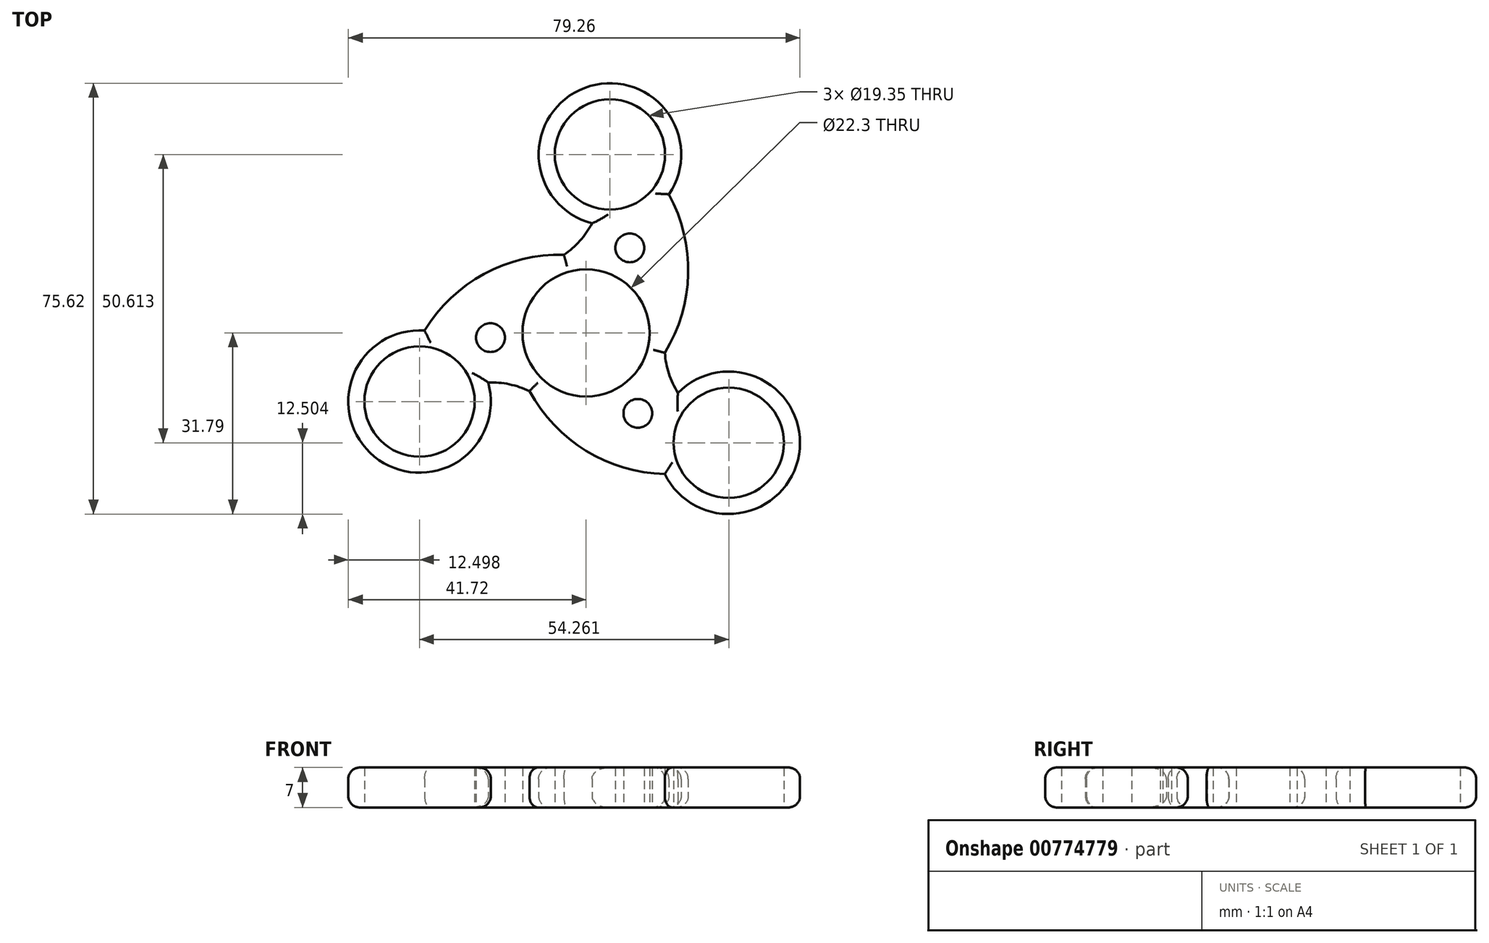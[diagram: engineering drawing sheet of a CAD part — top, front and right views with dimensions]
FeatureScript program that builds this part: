
annotation { "Feature Type Name" : "Feature", "Feature Type Description" : "" }
export const myFeature = defineFeature(function(context is Context, id is Id, definition is map)
    precondition{}
    {
        {
            var Q0;
            Q0=qCreatedBy(makeId("Top.planeOp"),FACE);
            var sketch = newSketch(context, id + "F0", { "sketchPlane" : qUnion([Q0])});
            skCircle(sketch, "E0", {"center": v(0, 0) * mm, "radius": 11.15 * mm});
            skArc(sketch, "E1", {"start": v(-9.94, -10.23) * mm, "mid": v(-0.01, -20.67) * mm, "end": v(13.8, -24.76) * mm});
            skArc(sketch, "E2", {"start": v(13.83, -3.5) * mm, "mid": v(14.54, -7.15) * mm, "end": v(16.13, -10.52) * mm});
            skCircle(sketch, "E3", {"center": v(25.04, -19.29) * mm, "radius": 9.68 * mm});
            skArc(sketch, "E4", {"start": v(13.8, -24.76) * mm, "mid": v(37.38, -21.3) * mm, "end": v(16.13, -10.52) * mm});
            skArc(sketch, "E5.1.0", {"start": v(-3.9, 13.72) * mm, "mid": v(-1.08, 16.16) * mm, "end": v(1.05, 19.23) * mm});
            skCircle(sketch, "E5.1.1", {"center": v(4.18, 31.33) * mm, "radius": 9.68 * mm});
            skArc(sketch, "E5.1.2", {"start": v(14.54, 24.34) * mm, "mid": v(-0.24, 43.02) * mm, "end": v(1.05, 19.23) * mm});
            skArc(sketch, "E5.1.3", {"start": v(13.83, -3.5) * mm, "mid": v(17.91, 10.33) * mm, "end": v(14.54, 24.34) * mm});
            skArc(sketch, "E5.2.0", {"start": v(-9.94, -10.23) * mm, "mid": v(-13.46, -9.01) * mm, "end": v(-17.17, -8.7) * mm});
            skCircle(sketch, "E5.2.1", {"center": v(-29.22, -12.04) * mm, "radius": 9.68 * mm});
            skArc(sketch, "E5.2.2", {"start": v(-28.35, 0.43) * mm, "mid": v(-37.13, -21.72) * mm, "end": v(-17.17, -8.7) * mm});
            skArc(sketch, "E5.2.3", {"start": v(-3.9, 13.72) * mm, "mid": v(-17.9, 10.35) * mm, "end": v(-28.35, 0.43) * mm});
            skPoint(sketch, "E6.trimOffspring.end.orphan", {"position": v(14, 0) * mm});
            skPoint(sketch, "E7.orphan", {"position": v(13.34, -4.26) * mm});
            skPoint(sketch, "E8.orphan", {"position": v(-7, -12.12) * mm});
            skPoint(sketch, "E9.orphan", {"position": v(-10.36, -9.42) * mm});
            skPoint(sketch, "E10.orphan", {"position": v(-7, 12.12) * mm});
            skPoint(sketch, "E11.orphan", {"position": v(-2.98, 13.68) * mm});
            skCircle(sketch, "E12", {"center": v(7.68, 14.94) * mm, "radius": 2.53 * mm});
            skCircle(sketch, "E13.1.0", {"center": v(-16.78, -0.82) * mm, "radius": 2.53 * mm});
            skCircle(sketch, "E13.2.0", {"center": v(9.1, -14.12) * mm, "radius": 2.53 * mm});
            skSolve(sketch);
        }
        {
            var Q0;
            Q0 = qSketchRegion(id + "F0", true);
            extrude(context, id + "F1", {"entities" : qUnion([Q0]), "depth" : 7 * mm, "offsetDistance" : 25 * mm});
        }
        {
            var Q0;
            Q0=makeQuery(id+"F1.opExtrude","CAP_EDGE",EDGE,{"disambiguationData":[OSD([sQuery(id+"F0.wireOp",EDGE,"E5.2.2")])],"isStart":false});
            var Q1;
            Q1=makeQuery(id+"F1.opExtrude","CAP_EDGE",EDGE,{"disambiguationData":[OSD([sQuery(id+"F0.wireOp",EDGE,"E5.2.2")])],"isStart":true});
            var Q2;
            Q2=makeQuery(id+"F1.opExtrude","CAP_EDGE",EDGE,{"disambiguationData":[OSD([sQuery(id+"F0.wireOp",EDGE,"E5.2.0")])],"isStart":true});
            var Q3;
            Q3=makeQuery(id+"F1.opExtrude","CAP_EDGE",EDGE,{"disambiguationData":[OSD([sQuery(id+"F0.wireOp",EDGE,"E5.2.0")])],"isStart":false});
            var Q4;
            Q4=makeQuery(id+"F1.opExtrude","CAP_EDGE",EDGE,{"disambiguationData":[OSD([sQuery(id+"F0.wireOp",EDGE,"E1")])],"isStart":false});
            var Q5;
            Q5=makeQuery(id+"F1.opExtrude","CAP_EDGE",EDGE,{"disambiguationData":[OSD([sQuery(id+"F0.wireOp",EDGE,"E4")])],"isStart":true});
            var Q6;
            Q6=makeQuery(id+"F1.opExtrude","CAP_EDGE",EDGE,{"disambiguationData":[OSD([sQuery(id+"F0.wireOp",EDGE,"E4")])],"isStart":false});
            var Q7;
            Q7=makeQuery(id+"F1.opExtrude","CAP_EDGE",EDGE,{"disambiguationData":[OSD([sQuery(id+"F0.wireOp",EDGE,"E2")])],"isStart":false});
            var Q8;
            Q8=makeQuery(id+"F1.opExtrude","CAP_EDGE",EDGE,{"disambiguationData":[OSD([sQuery(id+"F0.wireOp",EDGE,"E5.1.3")])],"isStart":false});
            var Q9;
            Q9=makeQuery(id+"F1.opExtrude","CAP_EDGE",EDGE,{"disambiguationData":[OSD([sQuery(id+"F0.wireOp",EDGE,"E5.1.3")])],"isStart":true});
            var Q10;
            Q10=makeQuery(id+"F1.opExtrude","CAP_EDGE",EDGE,{"disambiguationData":[OSD([sQuery(id+"F0.wireOp",EDGE,"E1")])],"isStart":true});
            var Q11;
            Q11=makeQuery(id+"F1.opExtrude","CAP_EDGE",EDGE,{"disambiguationData":[OSD([sQuery(id+"F0.wireOp",EDGE,"E2")])],"isStart":true});
            var Q12;
            Q12=makeQuery(id+"F1.opExtrude","CAP_EDGE",EDGE,{"disambiguationData":[OSD([sQuery(id+"F0.wireOp",EDGE,"E5.1.2")])],"isStart":true});
            var Q13;
            Q13=makeQuery(id+"F1.opExtrude","CAP_EDGE",EDGE,{"disambiguationData":[OSD([sQuery(id+"F0.wireOp",EDGE,"E5.1.2")])],"isStart":false});
            var Q14;
            Q14=makeQuery(id+"F1.opExtrude","CAP_EDGE",EDGE,{"disambiguationData":[OSD([sQuery(id+"F0.wireOp",EDGE,"E5.2.3")])],"isStart":true});
            var Q15;
            Q15=makeQuery(id+"F1.opExtrude","CAP_EDGE",EDGE,{"disambiguationData":[OSD([sQuery(id+"F0.wireOp",EDGE,"E5.2.3")])],"isStart":false});
            var Q16;
            Q16=makeQuery(id+"F1.opExtrude","CAP_EDGE",EDGE,{"disambiguationData":[OSD([sQuery(id+"F0.wireOp",EDGE,"E5.1.0")])],"isStart":false});
            var Q17;
            Q17=makeQuery(id+"F1.opExtrude","CAP_EDGE",EDGE,{"disambiguationData":[OSD([sQuery(id+"F0.wireOp",EDGE,"E5.1.0")])],"isStart":true});
            fillet(context, id + "F2", {"entities" : qUnion([Q0, Q1, Q2, Q3, Q4, Q5, Q6, Q7, Q8, Q9, Q10, Q11, Q12, Q13, Q14, Q15, Q16, Q17]), "radius" : 2 * mm, "tangentPropagation" : true, "allowEdgeOverflow" : false});
        }
    });
